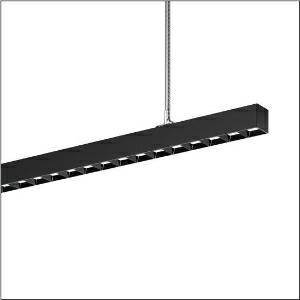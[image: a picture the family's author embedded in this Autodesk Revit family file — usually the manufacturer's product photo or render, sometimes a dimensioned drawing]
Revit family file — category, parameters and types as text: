
# Revit family: silica_r__21_51mx32dc3dbb_53cb
name_source: partatom
category: Lighting Fixtures
units: mm (PartAtom-declared; Revit-internal decimal feet)

## family parameters
Cut with Voids When Loaded = No
Host = Face
Light Source = No
Part Type = Normal
Room Calculation Point = No
Round Connector Dimension = Use Diameter
Shared = No

## types (1)
- --- (1 x LED, 18220 lm, 113 W, 3000K)
    Apparent Load = 113 VA
    CIE Flux Codes = 86 99 100 59 100
    Color Rendering = 80
    Color Temperature = 3000K
    Default Elevation = 1800 mm
    Description = Silica® 21, office luminaire, primary light control with darklight reflector, of PMMA, black, CAT 2 (L<= 3000cd/m²), light emission: direct/indirect distribution, primary light characteristic: symmetric, installation type: suspended mounting, LED, rated luminous flux: 18.220lm, luminous efficacy: 161lm/W, light colour: 830, colour temperature: 3000K, control gear: DALI 2, with terminal, 3+2-pole, max. 2.5mm², mains connection: 220..240V, AC, 50/60Hz, rated input power: 113W, luminaire housing, of aluminium, matt jet black (RAL 9005), length: 3.004mm, width: 53mm, height: 53mm, protection rating (complete): IP20, insulation class (complete): insulation class I (protective earthing), certification: CE, permissible operating ambient temperature: 0..+35°C, standard: EN 50419, packaging unit: 1 piece
    Height = 53 mm
    Lamp = 1 x LED
    Lamp Light Flux = 18220 lm
    Lamp Power = 113 W
    Lamp count = 1
    Length = 3004 mm
    Luminous efficacy = 161 lm/W
    Manufacturer = Siteco
    ModVariant = No
    Model = 51MX32DC3DBB
    Mounting Place = Ceiling
    Mounting Type = Pendant
    Number of Poles = 1
    OnlyDefault = Yes
    Power Factor = 1
    Product Name = Silica® 21
    Product group = office luminaire | ceiling pendant
    ProductGroupID = 904
    Protection Class = Protection class I
    Protection Degree = IP 20
    RLX_Detail_Level = 1
    RLX_Emergency_Light_Flux = 0 lm
    RLX_Emergency_Type = 0
    RLX_Emergency_Type_DB = No
    RlxData = <blob elided: 66713 chars, md5=a9f91fd9>
    Socket = socket
    Standby Power = 0 W
    System Light Flux = 18220 lm
    System Power = 113 W
    Type Comments = factory setting: luminous flux: 100 % | dim-lin: 254 | 391 mA
    Type Image = l_1335852.jpg
    URL = http://relux.com
    VarID = @adj_122068
    Voltage = 0 V
    Weight = 0.00 kg
    Width = 53 mm

## geometry (parser evidence)
native form markers: Blend x4, Sweep x15
no freeform markers — native parametric forms only
